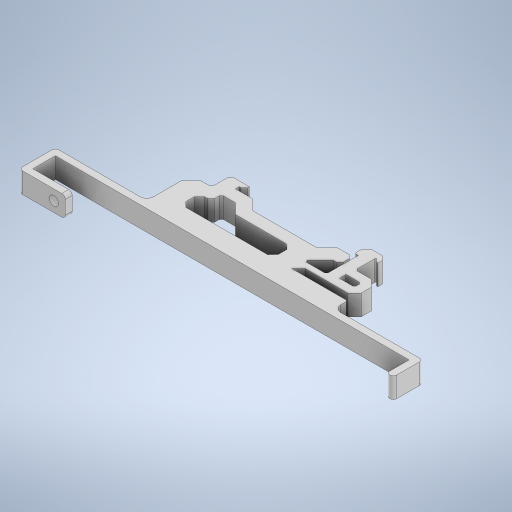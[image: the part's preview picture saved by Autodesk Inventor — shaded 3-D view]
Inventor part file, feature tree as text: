
AUTODESK INVENTOR PART (.ipt)
format: ipt  version: 2024 (Build 280153000, 153)  size: 462,336 bytes
history: native  units: in
note: dims shown in document units (in); Inventor stores cm internally (conversion verified against a paired STEP export)
features: extrude x3, sketch x3, fillet x2, projected_geometry x1
ambient origin geometry x8: Origin, YZ Plane, XZ Plane, XY Plane, X Axis, Y Axis, Z Axis, Center Point
bodies: Solid1 (feature_tree)
feature tree (9):
  extrude  "Extrusion1"  Depth=0.2362in TaperAngle=0.0deg
  extrude  "Extrusion2"  Depth=0.0787in
  fillet  "Fillet3"  Radius=0.3996in
  extrude  "Extrusion3"  Depth=0.2362in
  fillet  "Fillet4"  Radius=0.1181in
  sketch  "Sketch1"  dims[d8=0.2362in d9=0.0in d14=0.2362in d15=0.0in]
  sketch  "Sketch2"  dims[d18=0.3758in d19=0.1566in d20=0.1762in d21=0.1957in d22=0.1387in d23=0.1174in d24=0.0391in d25=0.0157in d26=2.1217in d27=0.0973in d28=0.0587in d29=0.0587in d30=0.0548in d31=0.0235in d32=0.9395in d33=0.0587in d34=0.0973in d35=0.5854in d36=0.1174in d37=0.7438in d38=0.1174in d39=0.1174in d40=0.137in d41=0.1475in d42=0.0277in d43=0.2143in d44=0.3464in d45=0.0196in d46=0.0626in d47=0.0137in d48=0.0274in d49=0.0607in d50=0.1213in d51=0.047in d52=0.0509in d53=0.0157in d54=0.0356in d55=0.0094in d56=0.2063in d57=0.0196in d58=0.1664in d59=0.0783in d60=0.1174in d61=0.0783in d62=0.4893in d63=0.0783in d64=0.6302in d65=0.0156in d66=0.1253in d67=0.1174in d68=0.1174in d69=0.1174in d70=0.0391in d71=0.0391in d72=0.0391in d73=0.1475in d74=0.0695in d75=0.0391in d76=0.0391in d77=0.0196in d78=0.0196in d79=0.0196in d80=0.0196in d81=0.0196in d82=0.0658in d83=0.0235in d84=0.0587in d85=0.0391in d86=0.0391in d87=0.0391in d88=0.0626in d89=0.0548in d90=0.0156in d91=0.0471in d92=0.0607in d93=0.0137in d94=0.0196in d95=0.094in d96=0.0196in d97=0.0156in d98=0.1376in d99=0.0352in d100=0.2349in d101=0.1566in d102=0.3568in d103=0.1566in d104=0.0115in d105=0.0156in d106=0.0772in d107=0.1751in d108=0.0984in d109=0.118in]
  sketch  "Sketch3"  dims[d110=4.0669in d111=0.2598in d112=0.0787in d113=0.0787in d114=0.0787in d115=0.0787in d116=0.5305in d117=0.2598in d118=0.1043in d119=0.3996in d120=0.2362in d121=0.1181in d122=0.0394in d123=4.2244in d124=1.0514in d125=0.2362in d126=0.0in d127=0.0787in]
  projected_geometry  "Projected Loop2"
